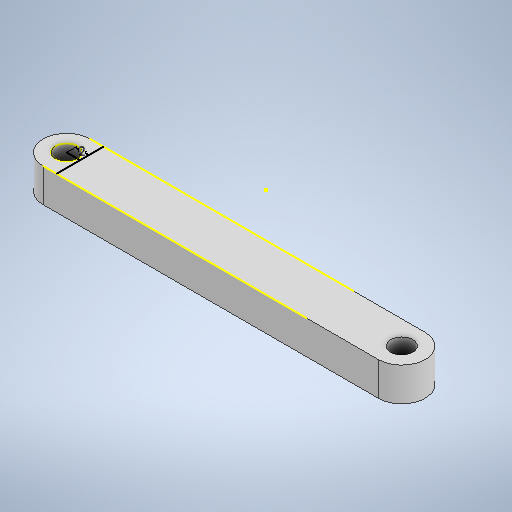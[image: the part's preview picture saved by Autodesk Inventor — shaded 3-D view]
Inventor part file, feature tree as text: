
AUTODESK INVENTOR PART (.ipt)
format: ipt  version: 2025.1 (Build 291241020, 241B)  size: 329,216 bytes
history: native  units: mm
features: sketch x6, move_body x4, extrude x3, split x3, boolean_combine x3, other x1, fillet x1, plane x1, imported_body x1
ambient origin geometry x8: Origin, YZ Plane, XZ Plane, XY Plane, X Axis, Y Axis, Z Axis, Center Point
bodies: Solid1 (feature_tree), Solid2 (feature_tree), Solid3 (feature_tree), Solid4 (feature_tree), Solid5 (feature_tree), Solid6 (feature_tree), Solid7 (feature_tree), Solid8 (feature_tree)
feature tree (23):
  other  "Repaired Geometry1"
  extrude  "Extrusion1"  Depth=7.0mm
  fillet  "Fillet1"  Radius=3.3mm
  move_body  "Move Body1"
  split  "Split1"
  move_body  "Move Body2"
  boolean_combine  "Combine1"
  sketch  "Sketch4"  dims[d5=3.5mm d6=5.0mm d7=0.0mm]
  plane  "Work Plane1"
  split  "Split2"
  split  "Split3"
  move_body  "Move Body3"
  move_body  "Move Body4"
  sketch  "Sketch5"  dims[d8=3.5mm]
  sketch  "Sketch6"  dims[d9=0.0mm d10=0.0mm d11=10.0mm]
  extrude  "Extrusion2"  Depth=3.5mm
  extrude  "Extrusion3"  Depth=5.0mm TaperAngle=0.0deg
  boolean_combine  "Combine2"
  boolean_combine  "Combine3"
  sketch  "Sketch7"  dims[d12=-0.1mm d13=0.0mm d14=0.0mm d15=2.0mm d16=90.0deg d17=22.5mm d18=0.0mm d19=0.0mm d20=10.7mm d21=0.0mm d22=0.0mm d23=10.0mm d24=0.0mm d25=10.0mm d26=0.0mm]
  sketch  "Sketch1"  dims[d0=7.0mm d1=39.4mm d2=3.3mm]
  imported_body  "Base1"
  sketch  "Sketch2"  dims[d3=3.3mm d4=3.5mm]
